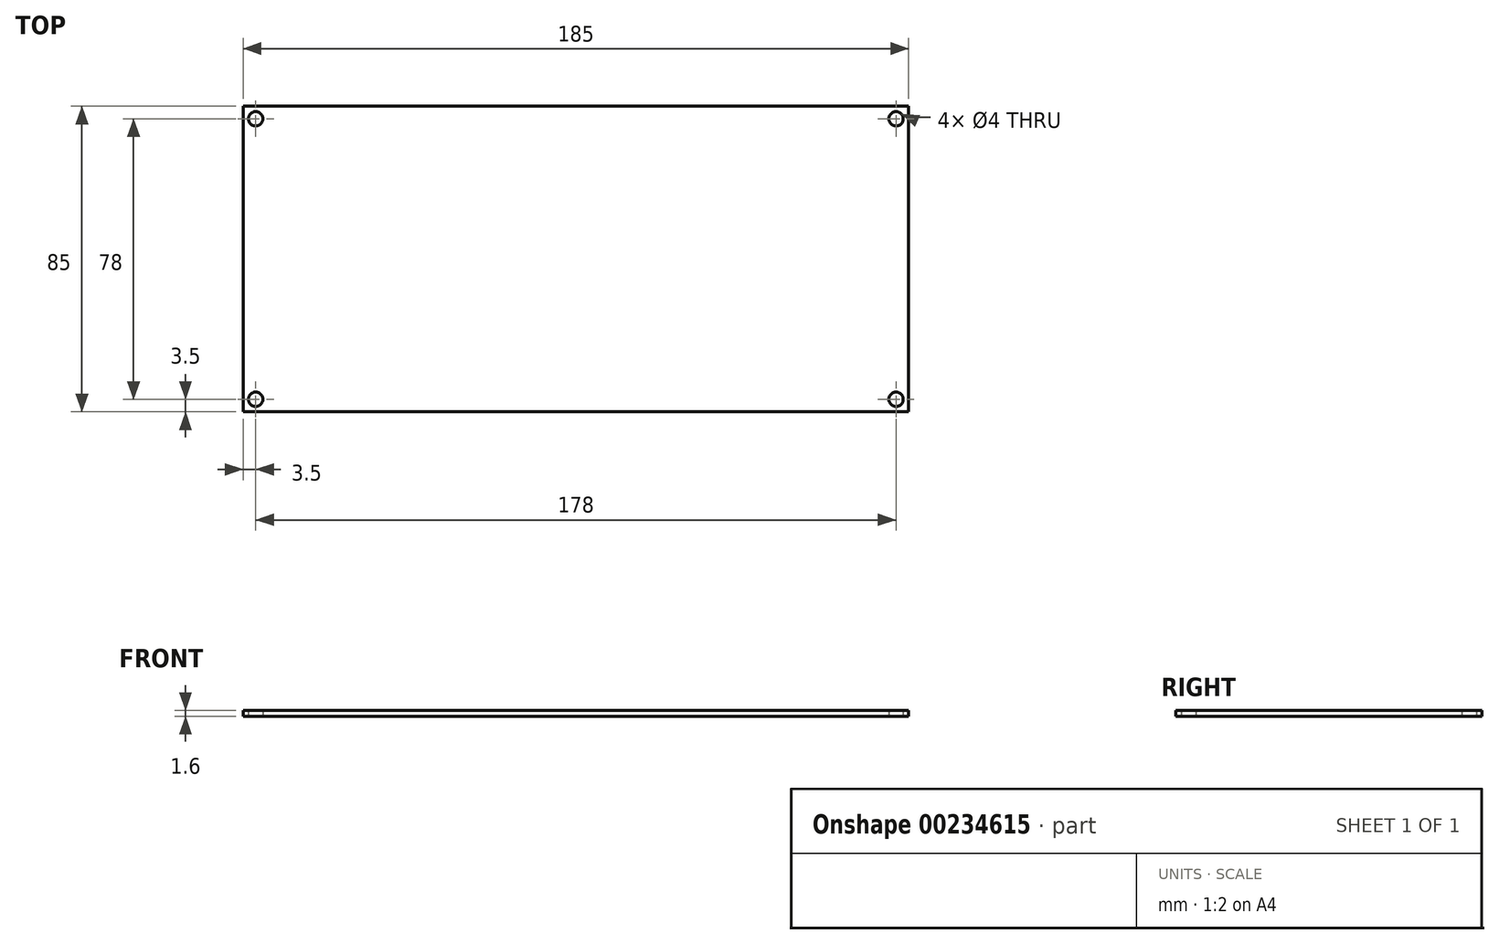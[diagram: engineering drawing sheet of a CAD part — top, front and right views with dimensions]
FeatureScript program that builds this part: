
annotation { "Feature Type Name" : "Feature", "Feature Type Description" : "" }
export const myFeature = defineFeature(function(context is Context, id is Id, definition is map)
    precondition{}
    {
        {
            var Q0;
            Q0=qCreatedBy(makeId("Top.planeOp"),FACE);
            var sketch = newSketch(context, id + "F0", { "sketchPlane" : qUnion([Q0])});
            skLineSegment(sketch, "E0.bottom", {"start": v(92.5, 42.5) * mm, "end": v(-92.5, 42.5) * mm});
            skLineSegment(sketch, "E0.top", {"start": v(92.5, -42.5) * mm, "end": v(-92.5, -42.5) * mm});
            skLineSegment(sketch, "E0.left", {"start": v(92.5, 42.5) * mm, "end": v(92.5, -42.5) * mm});
            skLineSegment(sketch, "E0.right", {"start": v(-92.5, 42.5) * mm, "end": v(-92.5, -42.5) * mm});
            skPoint(sketch, "E0.middle", {"position": v(0, 0) * mm});
            skCircle(sketch, "E1", {"center": v(-89, 39) * mm, "radius": 2 * mm});
            skCircle(sketch, "E2.MirrorC", {"center": v(89, 39) * mm, "radius": 2 * mm});
            skCircle(sketch, "E3.MirrorC", {"center": v(-89, -39) * mm, "radius": 2 * mm});
            skCircle(sketch, "E4.MirrorC", {"center": v(89, -39) * mm, "radius": 2 * mm});
            skSolve(sketch);
        }
        {
            var Q0;
            Q0 = qSketchRegion(id + "F0", true);
            extrude(context, id + "F1", {"entities" : qUnion([Q0]), "depth" : 1.6 * mm});
        }
    });
